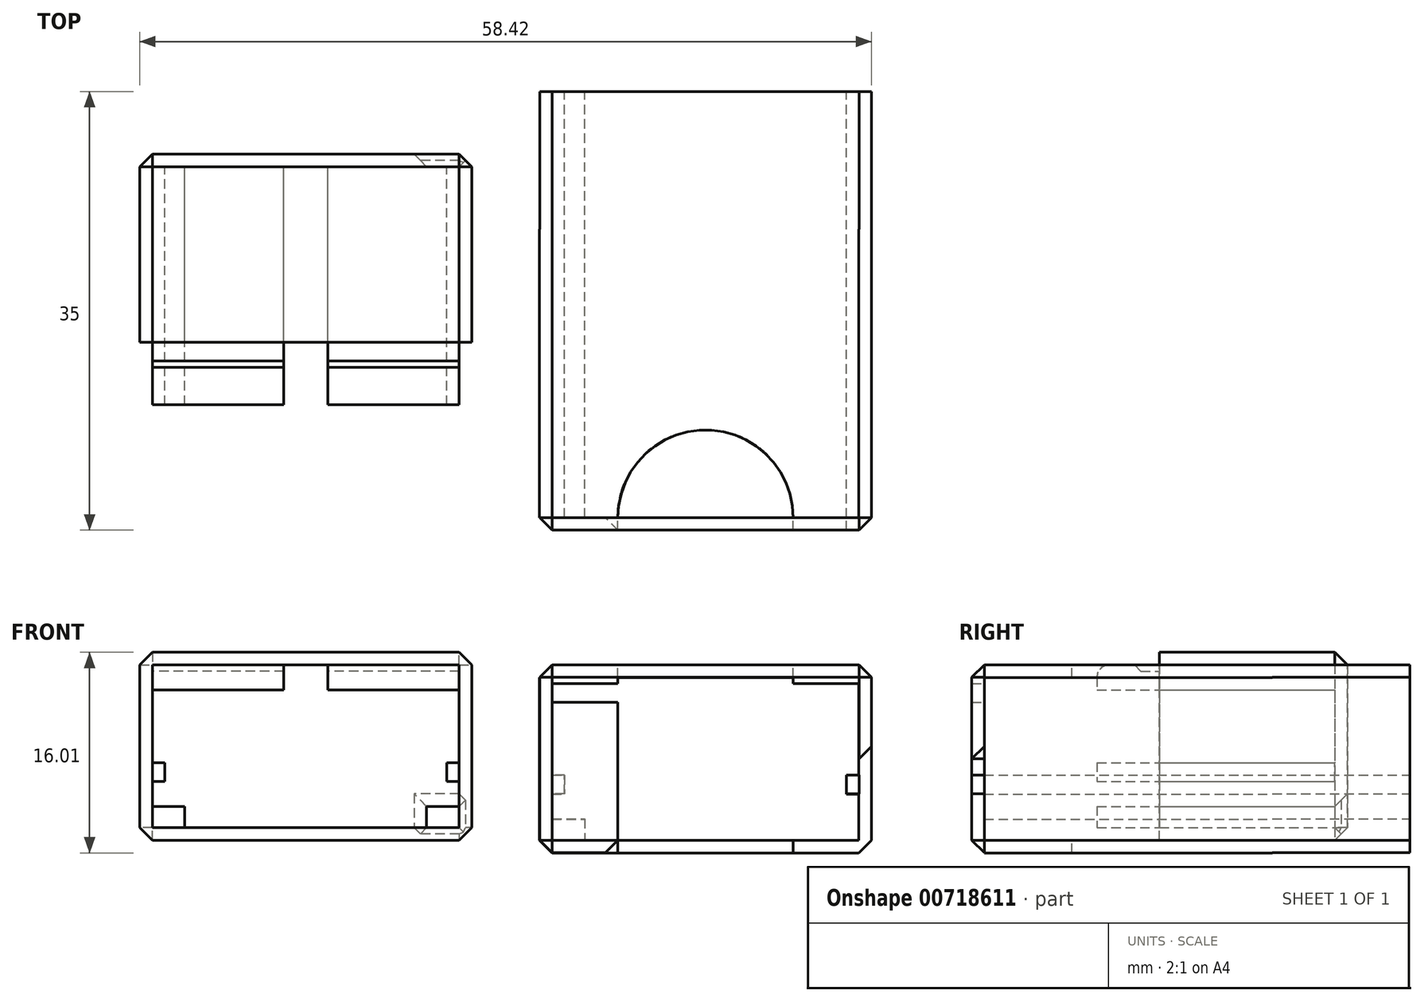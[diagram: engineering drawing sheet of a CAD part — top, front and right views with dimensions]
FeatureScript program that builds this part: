
annotation { "Feature Type Name" : "Feature", "Feature Type Description" : "" }
export const myFeature = defineFeature(function(context is Context, id is Id, definition is map)
    precondition{}
    {
        {
            var Q0;
            Q0=qCreatedBy(makeId("Front.planeOp"),FACE);
            var sketch = newSketch(context, id + "F0", { "sketchPlane" : qUnion([Q0])});
            skLineSegment(sketch, "E0.bottom", {"start": v(0, 0) * mm, "end": v(-24.5, 0) * mm});
            skLineSegment(sketch, "E0.top", {"start": v(0, -13) * mm, "end": v(-24.5, -13) * mm});
            skLineSegment(sketch, "E0.left", {"start": v(0, 0) * mm, "end": v(0, -13) * mm});
            skLineSegment(sketch, "E0.right", {"start": v(-24.5, 0) * mm, "end": v(-24.5, -13) * mm});
            skLineSegment(sketch, "E1", {"start": v(0, 0) * mm, "end": v(0, 1) * mm});
            skLineSegment(sketch, "E2", {"start": v(-25.5, 1) * mm, "end": v(-25.5, -14) * mm});
            skLineSegment(sketch, "E3", {"start": v(-25.5, -14) * mm, "end": v(1, -14) * mm});
            skLineSegment(sketch, "E4", {"start": v(1, -14) * mm, "end": v(1, 1) * mm});
            skLineSegment(sketch, "E5", {"start": v(-25.5, 1) * mm, "end": v(1, 1) * mm});
            skLineSegment(sketch, "E6", {"start": v(0, -13) * mm, "end": v(0, -9.3) * mm});
            skLineSegment(sketch, "E7", {"start": v(-24.5, -9.3) * mm, "end": v(-23.5, -9.3) * mm});
            skLineSegment(sketch, "E8", {"start": v(-23.5, -11.3) * mm, "end": v(-24.5, -11.3) * mm});
            skLineSegment(sketch, "E9", {"start": v(0, -9.3) * mm, "end": v(0, -11.3) * mm});
            skLineSegment(sketch, "E10", {"start": v(0, -11.3) * mm, "end": v(-1, -11.3) * mm});
            skLineSegment(sketch, "E11", {"start": v(-1, -9.3) * mm, "end": v(0, -9.3) * mm});
            skLineSegment(sketch, "E12", {"start": v(-23.5, -9.3) * mm, "end": v(-23.5, -7.8) * mm});
            skLineSegment(sketch, "E13", {"start": v(-23.5, -7.8) * mm, "end": v(-24.5, -7.8) * mm});
            skLineSegment(sketch, "E14", {"start": v(-24.5, -11.3) * mm, "end": v(-24.5, -9.3) * mm});
            skLineSegment(sketch, "E15", {"start": v(-1, -9.3) * mm, "end": v(-1, -7.8) * mm});
            skLineSegment(sketch, "E16", {"start": v(-1, -7.8) * mm, "end": v(0, -7.8) * mm});
            skLineSegment(sketch, "E17", {"start": v(-24.5, 0) * mm, "end": v(-24.5, -2) * mm});
            skLineSegment(sketch, "E18", {"start": v(-12.25, 0) * mm, "end": v(-10.5, 0) * mm});
            skLineSegment(sketch, "E19", {"start": v(-10.5, 0) * mm, "end": v(-14, 0) * mm});
            skLineSegment(sketch, "E20", {"start": v(-14, 0) * mm, "end": v(-14, -2) * mm});
            skLineSegment(sketch, "E21", {"start": v(-14, -2) * mm, "end": v(-24.5, -2) * mm});
            skLineSegment(sketch, "E22", {"start": v(-10.5, 0) * mm, "end": v(-10.5, -2) * mm});
            skLineSegment(sketch, "E23", {"start": v(-10.5, -2) * mm, "end": v(0, -2) * mm});
            skLineSegment(sketch, "E24", {"start": v(-24.5, -11.3) * mm, "end": v(-21.9, -11.3) * mm});
            skLineSegment(sketch, "E25", {"start": v(-21.9, -11.3) * mm, "end": v(-21.9, -13) * mm});
            skLineSegment(sketch, "E26", {"start": v(0, -11.3) * mm, "end": v(-2.6, -11.3) * mm});
            skLineSegment(sketch, "E27", {"start": v(-2.6, -11.3) * mm, "end": v(-2.6, -13) * mm});
            skLineSegment(sketch, "E28", {"start": v(0, -2) * mm, "end": v(0, -0.5) * mm});
            skLineSegment(sketch, "E29", {"start": v(0, -0.5) * mm, "end": v(-10.5, -0.5) * mm});
            skLineSegment(sketch, "E30", {"start": v(-14, -2) * mm, "end": v(-14, -0.5) * mm});
            skLineSegment(sketch, "E31", {"start": v(-14, -0.5) * mm, "end": v(-24.5, -0.5) * mm});
            skSolve(sketch);
        }
        {
            var Q0;
            Q0 = qSketchRegion(id + "F0", true);
            var Q1;
            {var subQ3=sQuery(id+"F0.wireOp",EDGE,"E20");Q1=makeQuery(id+"F0.imprint","IMPRINT",FACE,{"disambiguationData":[TD([[makeQuery(id+"F0.imprint","IMPRINT",EDGE,{"derivedFrom":subQ3}),-1.0]])]});}
            var Q2;
            {var subQ5=sQuery(id+"F0.wireOp",EDGE,"E29");Q2=makeQuery(id+"F0.imprint","IMPRINT",FACE,{"disambiguationData":[TD([[makeQuery(id+"F0.imprint","IMPRINT",EDGE,{"derivedFrom":subQ5}),-1.0]])]});}
            extrude(context, id + "F1", {"entities" : qUnion([Q0, Q1, Q2]), "depth" : 15 * mm, "offsetDistance" : 25 * mm});
        }
        {
            var Q0;
            {var subQ0=sQuery(id+"F0.wireOp",EDGE,"E21");Q0=makeQuery(id+"F0.imprint","IMPRINT",FACE,{"disambiguationData":[TD([[makeQuery(id+"F0.imprint","IMPRINT",EDGE,{"derivedFrom":subQ0}),-1.0]])]});}
            var Q1;
            {var subQ0=sQuery(id+"F0.wireOp",EDGE,"E23");Q1=makeQuery(id+"F0.imprint","IMPRINT",FACE,{"disambiguationData":[TD([[makeQuery(id+"F0.imprint","IMPRINT",EDGE,{"derivedFrom":subQ0}),1.0]])]});}
            var Q2;
            {var subQ0=sQuery(id+"F0.wireOp",EDGE,"E11");Q2=makeQuery(id+"F0.imprint","IMPRINT",FACE,{"disambiguationData":[TD([[makeQuery(id+"F0.imprint","IMPRINT",EDGE,{"derivedFrom":subQ0}),1.0]])]});}
            var Q3;
            {var subQ3=sQuery(id+"F0.wireOp",EDGE,"E6");Q3=makeQuery(id+"F0.imprint","IMPRINT",FACE,{"disambiguationData":[TD([[makeQuery(id+"F0.imprint","IMPRINT",EDGE,{"derivedFrom":subQ3}),1.0]])]});}
            var Q4;
            {var subQ0=sQuery(id+"F0.wireOp",EDGE,"E7");Q4=makeQuery(id+"F0.imprint","IMPRINT",FACE,{"disambiguationData":[TD([[makeQuery(id+"F0.imprint","IMPRINT",EDGE,{"derivedFrom":subQ0}),1.0]])]});}
            var Q5;
            {var subQ0=sQuery(id+"F0.wireOp",EDGE,"E25");Q5=makeQuery(id+"F0.imprint","IMPRINT",FACE,{"disambiguationData":[TD([[makeQuery(id+"F0.imprint","IMPRINT",EDGE,{"derivedFrom":subQ0}),-1.0]])]});}
            extrude(context, id + "F2", {"entities" : qUnion([Q0, Q1, Q2, Q3, Q4, Q5]), "operationType" : NewBodyOperationType.ADD, "depth" : 20 * mm, "offsetDistance" : 25 * mm});
        }
        {
            var Q0;
            {var subQ19=sQuery(id+"F0.wireOp",EDGE,"E2");Q0=makeQuery(id+"F0.imprint","IMPRINT",FACE,{"disambiguationData":[TD([[makeQuery(id+"F0.imprint","IMPRINT",EDGE,{"derivedFrom":subQ19}),1.0]])]});}
            var Q1;
            {var subQ3=sQuery(id+"F0.wireOp",EDGE,"E22");Q1=makeQuery(id+"F0.imprint","IMPRINT",FACE,{"disambiguationData":[TD([[makeQuery(id+"F0.imprint","IMPRINT",EDGE,{"derivedFrom":subQ3}),1.0]])]});}
            var Q2;
            {var subQ0=sQuery(id+"F0.wireOp",EDGE,"E17");Q2=makeQuery(id+"F0.imprint","IMPRINT",FACE,{"disambiguationData":[TD([[makeQuery(id+"F0.imprint","IMPRINT",EDGE,{"derivedFrom":subQ0}),1.0]])]});}
            var Q3;
            {var subQ0=sQuery(id+"F0.wireOp",EDGE,"E7");Q3=makeQuery(id+"F0.imprint","IMPRINT",FACE,{"disambiguationData":[TD([[makeQuery(id+"F0.imprint","IMPRINT",EDGE,{"derivedFrom":subQ0}),1.0]])]});}
            var Q4;
            {var subQ0=sQuery(id+"F0.wireOp",EDGE,"E25");Q4=makeQuery(id+"F0.imprint","IMPRINT",FACE,{"disambiguationData":[TD([[makeQuery(id+"F0.imprint","IMPRINT",EDGE,{"derivedFrom":subQ0}),-1.0]])]});}
            var Q5;
            {var subQ0=sQuery(id+"F0.wireOp",EDGE,"E11");Q5=makeQuery(id+"F0.imprint","IMPRINT",FACE,{"disambiguationData":[TD([[makeQuery(id+"F0.imprint","IMPRINT",EDGE,{"derivedFrom":subQ0}),1.0]])]});}
            var Q6;
            {var subQ1=sQuery(id+"F0.wireOp",EDGE,"E6");Q6=makeQuery(id+"F0.imprint","IMPRINT",FACE,{"disambiguationData":[TD([[makeQuery(id+"F0.imprint","IMPRINT",EDGE,{"derivedFrom":subQ1}),1.0]])]});}
            var Q7;
            Q7=makeQuery(id+"F0.imprint","IMPRINT",FACE,{"disambiguationData":[TD([[makeQuery(id+"F0.imprint","IMPRINT",EDGE,{"derivedFrom":sQuery(id+"F0.wireOp",EDGE,"E7")}),-1.0]])]});
            extrude(context, id + "F3", {"entities" : qUnion([Q0, Q1, Q2, Q3, Q4, Q5, Q6, Q7]), "operationType" : NewBodyOperationType.ADD, "depth" : 1 * mm, "offsetDistance" : 25 * mm});
        }
        {
            var Q0;
            {var subQ0=sQuery(id+"F0.wireOp",EDGE,"E5");var subQ1=sQuery(id+"F0.wireOp",EDGE,"E4");var subQ2=sQuery(id+"F0.wireOp",EDGE,"E3");var subQ3=sQuery(id+"F0.wireOp",EDGE,"E2");var subQ4=sQuery(id+"F0.wireOp",EDGE,"E0.right");var subQ5=sQuery(id+"F0.wireOp",EDGE,"E0.left");var subQ6=sQuery(id+"F0.wireOp",EDGE,"E0.top");var subQ7=sQuery(id+"F0.wireOp",EDGE,"E6");var subQ8=sQuery(id+"F0.wireOp",EDGE,"E17");var subQ9=sQuery(id+"F0.wireOp",EDGE,"E0.bottom");Q0=makeQuery(id+"F3.boolean.opBoolean","MERGE",FACE,{"derivedFrom":[makeQuery(id+"F2.boolean.opBoolean","MERGE",FACE,{"derivedFrom":[makeQuery(id+"F1.opExtrude","CAP_FACE",FACE,{"disambiguationData":[OSD([subQ9,subQ6,subQ5,subQ4,subQ3,subQ2,subQ1,subQ0,subQ7,sQuery(id+"F0.wireOp",EDGE,"E9"),sQuery(id+"F0.wireOp",EDGE,"E14"),subQ8,sQuery(id+"F0.wireOp",EDGE,"E19")])],"isStart":true}),makeQuery(id+"F2.opExtrude","CAP_FACE",FACE,{"disambiguationData":[OSD([subQ9,subQ5,sQuery(id+"F0.wireOp",EDGE,"E22"),sQuery(id+"F0.wireOp",EDGE,"E23")])],"isStart":true}),makeQuery(id+"F2.opExtrude","CAP_FACE",FACE,{"disambiguationData":[OSD([subQ9,subQ8,sQuery(id+"F0.wireOp",EDGE,"E20"),sQuery(id+"F0.wireOp",EDGE,"E21")])],"isStart":true}),makeQuery(id+"F2.opExtrude","CAP_FACE",FACE,{"disambiguationData":[OSD([subQ6,subQ7,sQuery(id+"F0.wireOp",EDGE,"E26"),sQuery(id+"F0.wireOp",EDGE,"E27")])],"isStart":true}),makeQuery(id+"F2.opExtrude","CAP_FACE",FACE,{"disambiguationData":[OSD([subQ6,subQ4,sQuery(id+"F0.wireOp",EDGE,"E24"),sQuery(id+"F0.wireOp",EDGE,"E25")])],"isStart":true}),makeQuery(id+"F2.opExtrude","CAP_FACE",FACE,{"disambiguationData":[OSD([subQ5,sQuery(id+"F0.wireOp",EDGE,"E11"),sQuery(id+"F0.wireOp",EDGE,"E15"),sQuery(id+"F0.wireOp",EDGE,"E16")])],"isStart":true}),makeQuery(id+"F2.opExtrude","CAP_FACE",FACE,{"disambiguationData":[OSD([subQ4,sQuery(id+"F0.wireOp",EDGE,"E7"),sQuery(id+"F0.wireOp",EDGE,"E12"),sQuery(id+"F0.wireOp",EDGE,"E13")])],"isStart":true})]}),makeQuery(id+"F3.opExtrude","CAP_FACE",FACE,{"disambiguationData":[OSD([subQ3,subQ2,subQ1,subQ0])],"isStart":true})]});}
            var Q1;
            Q1=makeQuery(id+"F1.opExtrude","SWEPT_EDGE",EDGE,{"disambiguationData":[OSD([sQuery(id+"F0.wireOp",EDGE,"E2"),sQuery(id+"F0.wireOp",EDGE,"E3")])]});
            var Q2;
            Q2=makeQuery(id+"F1.opExtrude","SWEPT_EDGE",EDGE,{"disambiguationData":[OSD([sQuery(id+"F0.wireOp",EDGE,"E3"),sQuery(id+"F0.wireOp",EDGE,"E4")])]});
            var Q3;
            Q3=makeQuery(id+"F1.opExtrude","SWEPT_EDGE",EDGE,{"disambiguationData":[OSD([sQuery(id+"F0.wireOp",EDGE,"E2"),sQuery(id+"F0.wireOp",EDGE,"E5")])]});
            var Q4;
            Q4=makeQuery(id+"F1.opExtrude","SWEPT_EDGE",EDGE,{"disambiguationData":[OSD([sQuery(id+"F0.wireOp",EDGE,"E4"),sQuery(id+"F0.wireOp",EDGE,"E5")])]});
            chamfer(context, id + "F4", {"entities" : qUnion([Q0, Q1, Q2, Q3, Q4]), "width" : 1 * mm, "tangentPropagation" : true});
        }
        {
            var Q0;
            Q0=qCreatedBy(makeId("Front.planeOp"),FACE);
            cPlane(context, id + "F5", {"entities" : qUnion([Q0]), "cplaneType" : CPlaneType.OFFSET, "offset" : 16 * mm, "width" : 150 * mm, "height" : 150 * mm});
        }
        {
            var Q0;
            Q0=qCreatedBy(id+"F5.planeOp",FACE);
            var sketch = newSketch(context, id + "F6", { "sketchPlane" : qUnion([Q0])});
            skLineSegment(sketch, "E32.bottom", {"start": v(0, 0) * mm, "end": v(-10.5, 0) * mm});
            skLineSegment(sketch, "E32.top", {"start": v(0, -2) * mm, "end": v(-10.5, -2) * mm});
            skLineSegment(sketch, "E32.left", {"start": v(0, 0) * mm, "end": v(0, -2) * mm});
            skLineSegment(sketch, "E32.right", {"start": v(-10.5, 0) * mm, "end": v(-10.5, -2) * mm});
            skLineSegment(sketch, "E33", {"start": v(-10.5, 0) * mm, "end": v(-14, 0) * mm});
            skLineSegment(sketch, "E34.bottom", {"start": v(-14, 0) * mm, "end": v(-24.5, 0) * mm});
            skLineSegment(sketch, "E34.top", {"start": v(-14, -2) * mm, "end": v(-24.5, -2) * mm});
            skLineSegment(sketch, "E34.left", {"start": v(-14, 0) * mm, "end": v(-14, -2) * mm});
            skLineSegment(sketch, "E34.right", {"start": v(-24.5, 0) * mm, "end": v(-24.5, -2) * mm});
            skSolve(sketch);
        }
        {
            var Q0;
            Q0 = qSketchRegion(id + "F6", true);
            extrude(context, id + "F7", {"entities" : qUnion([Q0]), "operationType" : NewBodyOperationType.ADD, "depth" : 4 * mm, "offsetDistance" : 25 * mm});
        }
        {
            var Q0;
            Q0=makeQuery(id+"F7.opExtrude","CAP_EDGE",EDGE,{"disambiguationData":[OSD([sQuery(id+"F6.wireOp",EDGE,"E32.bottom")])],"isStart":false});
            var Q1;
            Q1=makeQuery(id+"F7.opExtrude","CAP_EDGE",EDGE,{"disambiguationData":[OSD([sQuery(id+"F6.wireOp",EDGE,"E34.bottom")])],"isStart":false});
            fillet(context, id + "F8", {"entities" : qUnion([Q0, Q1]), "radius" : 1 * mm, "tangentPropagation" : true, "allowEdgeOverflow" : false});
        }
        {
            var Q0;
            Q0=makeQuery(id+"F7.opExtrude","CAP_EDGE",EDGE,{"disambiguationData":[OSD([sQuery(id+"F6.wireOp",EDGE,"E32.bottom")])],"isStart":true});
            var Q1;
            Q1=makeQuery(id+"F7.opExtrude","CAP_EDGE",EDGE,{"disambiguationData":[OSD([sQuery(id+"F6.wireOp",EDGE,"E34.bottom")])],"isStart":true});
            chamfer(context, id + "F9", {"entities" : qUnion([Q0, Q1]), "width" : 1 * mm, "tangentPropagation" : true});
        }
        {
            var Q0;
            Q0=qCreatedBy(makeId("Front.planeOp"),FACE);
            var sketch = newSketch(context, id + "F10", { "sketchPlane" : qUnion([Q0])});
            skLineSegment(sketch, "E35.bottom", {"start": v(6.42, 0) * mm, "end": v(32.92, 0) * mm});
            skLineSegment(sketch, "E35.top", {"start": v(6.42, -15) * mm, "end": v(32.92, -15) * mm});
            skLineSegment(sketch, "E35.left", {"start": v(6.42, 0) * mm, "end": v(6.42, -15) * mm});
            skLineSegment(sketch, "E35.right", {"start": v(32.92, 0) * mm, "end": v(32.92, -15) * mm});
            skLineSegment(sketch, "E36", {"start": v(7.42, 0) * mm, "end": v(7.42, -1) * mm});
            skLineSegment(sketch, "E37", {"start": v(7.42, -14) * mm, "end": v(6.42, -14) * mm});
            skLineSegment(sketch, "E38", {"start": v(7.42, -1) * mm, "end": v(7.42, -14) * mm});
            skLineSegment(sketch, "E39.bottom", {"start": v(31.92, -1) * mm, "end": v(7.42, -1) * mm});
            skLineSegment(sketch, "E39.top", {"start": v(31.92, -14) * mm, "end": v(7.42, -14) * mm});
            skLineSegment(sketch, "E39.left", {"start": v(31.92, -1) * mm, "end": v(31.92, -14) * mm});
            skLineSegment(sketch, "E40", {"start": v(31.92, -14) * mm, "end": v(31.92, -10.3) * mm});
            skLineSegment(sketch, "E41", {"start": v(31.92, -10.3) * mm, "end": v(31.92, -12.3) * mm});
            skLineSegment(sketch, "E42", {"start": v(31.92, -10.3) * mm, "end": v(30.92, -10.3) * mm});
            skLineSegment(sketch, "E43", {"start": v(32.92, -7.5) * mm, "end": v(31.92, -7.5) * mm});
            skLineSegment(sketch, "E44", {"start": v(30.92, -10.3) * mm, "end": v(30.92, -8.8) * mm});
            skLineSegment(sketch, "E45", {"start": v(30.92, -8.8) * mm, "end": v(31.92, -8.8) * mm});
            skLineSegment(sketch, "E46", {"start": v(31.92, -14) * mm, "end": v(29.32, -14) * mm});
            skLineSegment(sketch, "E47", {"start": v(31.92, -12.3) * mm, "end": v(29.32, -12.3) * mm});
            skLineSegment(sketch, "E48", {"start": v(29.32, -12.3) * mm, "end": v(29.32, -14) * mm});
            skLineSegment(sketch, "E49", {"start": v(19.67, -1) * mm, "end": v(19.67, -14) * mm});
            skLineSegment(sketch, "E50.MirrorCS", {"start": v(8.42, -8.8) * mm, "end": v(7.42, -8.8) * mm});
            skLineSegment(sketch, "E51.MirrorCS", {"start": v(8.42, -10.3) * mm, "end": v(8.42, -8.8) * mm});
            skLineSegment(sketch, "E52.MirrorCS", {"start": v(7.42, -10.3) * mm, "end": v(8.42, -10.3) * mm});
            skLineSegment(sketch, "E53.MirrorCS", {"start": v(7.42, -12.3) * mm, "end": v(10.02, -12.3) * mm});
            skLineSegment(sketch, "E54.MirrorCS", {"start": v(10.02, -12.3) * mm, "end": v(10.02, -14) * mm});
            skLineSegment(sketch, "E55", {"start": v(19.67, -1) * mm, "end": v(19.67, -3) * mm});
            skLineSegment(sketch, "E56", {"start": v(17.92, -3) * mm, "end": v(17.92, -1) * mm});
            skLineSegment(sketch, "E57", {"start": v(17.92, -1) * mm, "end": v(17.92, -1.5) * mm});
            skLineSegment(sketch, "E58", {"start": v(17.92, -1.5) * mm, "end": v(7.42, -1.5) * mm});
            skLineSegment(sketch, "E59", {"start": v(7.42, -1.5) * mm, "end": v(7.42, -3) * mm});
            skLineSegment(sketch, "E60", {"start": v(31.92, -3) * mm, "end": v(31.92, -1.5) * mm});
            skLineSegment(sketch, "E61", {"start": v(31.92, -1.5) * mm, "end": v(21.42, -1.5) * mm});
            skLineSegment(sketch, "E62", {"start": v(21.42, -1.5) * mm, "end": v(21.42, -3) * mm});
            skLineSegment(sketch, "E63", {"start": v(21.42, -1.5) * mm, "end": v(21.42, -1) * mm});
            skLineSegment(sketch, "E64", {"start": v(21.42, -1) * mm, "end": v(21.42, -3) * mm});
            skLineSegment(sketch, "E65", {"start": v(7.42, -3) * mm, "end": v(17.92, -3) * mm});
            skLineSegment(sketch, "E66", {"start": v(21.42, -3) * mm, "end": v(31.92, -3) * mm});
            skSolve(sketch);
        }
        {
            var Q0;
            {var subQ10=sQuery(id+"F10.wireOp",EDGE,"E36");Q0=makeQuery(id+"F10.imprint","IMPRINT",FACE,{"disambiguationData":[TD([[makeQuery(id+"F10.imprint","IMPRINT",EDGE,{"derivedFrom":subQ10}),1.0]])]});}
            var Q1;
            {var subQ3=sQuery(id+"F10.wireOp",EDGE,"E35.top");Q1=makeQuery(id+"F10.imprint","IMPRINT",FACE,{"disambiguationData":[TD([[makeQuery(id+"F10.imprint","IMPRINT",EDGE,{"derivedFrom":subQ3}),1.0]])]});}
            var Q2;
            {var subQ0=sQuery(id+"F10.wireOp",EDGE,"E36");Q2=makeQuery(id+"F10.imprint","IMPRINT",FACE,{"disambiguationData":[TD([[makeQuery(id+"F10.imprint","IMPRINT",EDGE,{"derivedFrom":subQ0}),-1.0]])]});}
            var Q3;
            {var subQ0=sQuery(id+"F10.wireOp",EDGE,"E42");Q3=makeQuery(id+"F10.imprint","IMPRINT",FACE,{"disambiguationData":[TD([[makeQuery(id+"F10.imprint","IMPRINT",EDGE,{"derivedFrom":subQ0}),-1.0]])]});}
            var Q4;
            Q4=makeQuery(id+"F10.imprint","IMPRINT",FACE,{"disambiguationData":[TD([[makeQuery(id+"F10.imprint","IMPRINT",EDGE,{"derivedFrom":sQuery(id+"F10.wireOp",EDGE,"E40")}),1.0]])]});
            var Q5;
            {var subQ0=sQuery(id+"F10.wireOp",EDGE,"E50.MirrorCS");Q5=makeQuery(id+"F10.imprint","IMPRINT",FACE,{"disambiguationData":[TD([[makeQuery(id+"F10.imprint","IMPRINT",EDGE,{"derivedFrom":subQ0}),1.0]])]});}
            var Q6;
            {var subQ4=sQuery(id+"F10.wireOp",EDGE,"E53.MirrorCS");Q6=makeQuery(id+"F10.imprint","IMPRINT",FACE,{"disambiguationData":[TD([[makeQuery(id+"F10.imprint","IMPRINT",EDGE,{"derivedFrom":subQ4}),-1.0]])]});}
            var Q7;
            Q7=sQuery(id+"F10.wireOp",EDGE,"E35.bottom");
            var Q8;
            Q8=sQuery(id+"F10.wireOp",EDGE,"E35.right");
            var Q9;
            Q9=sQuery(id+"F10.wireOp",EDGE,"E39.left");
            extrude(context, id + "F11", {"entities" : qUnion([Q0, Q1, Q2, Q3, Q4, Q5, Q6]), "surfaceEntities" : qUnion([Q7, Q8, Q9]), "depth" : 6 * mm, "offsetDistance" : 25 * mm});
        }
        {
            var Q0;
            Q0=qCreatedBy(makeId("Front.planeOp"),FACE);
            cPlane(context, id + "F12", {"entities" : qUnion([Q0]), "cplaneType" : CPlaneType.OFFSET, "offset" : 6 * mm, "width" : 150 * mm, "height" : 150 * mm});
        }
        {
            var Q0;
            Q0=qCreatedBy(id+"F12.planeOp",FACE);
            var sketch = newSketch(context, id + "F13", { "sketchPlane" : qUnion([Q0])});
            skLineSegment(sketch, "E67.bottom", {"start": v(6.42, 0) * mm, "end": v(32.92, 0) * mm});
            skLineSegment(sketch, "E67.top", {"start": v(6.42, -15) * mm, "end": v(32.92, -15) * mm});
            skLineSegment(sketch, "E67.left", {"start": v(6.42, 0) * mm, "end": v(6.42, -15) * mm});
            skLineSegment(sketch, "E67.right", {"start": v(32.92, 0) * mm, "end": v(32.92, -15) * mm});
            skLineSegment(sketch, "E68", {"start": v(7.42, 0) * mm, "end": v(7.42, -1) * mm});
            skLineSegment(sketch, "E69", {"start": v(7.42, -14) * mm, "end": v(6.42, -14) * mm});
            skLineSegment(sketch, "E70", {"start": v(7.42, -1) * mm, "end": v(7.42, -14) * mm});
            skLineSegment(sketch, "E71.bottom", {"start": v(31.92, -1) * mm, "end": v(7.42, -1) * mm});
            skLineSegment(sketch, "E71.top", {"start": v(31.92, -14) * mm, "end": v(7.42, -14) * mm});
            skLineSegment(sketch, "E71.left", {"start": v(31.92, -1) * mm, "end": v(31.92, -14) * mm});
            skLineSegment(sketch, "E72", {"start": v(31.92, -14) * mm, "end": v(31.92, -10.3) * mm});
            skLineSegment(sketch, "E73", {"start": v(31.92, -10.3) * mm, "end": v(31.92, -12.3) * mm});
            skLineSegment(sketch, "E74", {"start": v(31.92, -10.3) * mm, "end": v(30.92, -10.3) * mm});
            skLineSegment(sketch, "E75", {"start": v(32.92, -7.5) * mm, "end": v(31.92, -7.5) * mm});
            skLineSegment(sketch, "E76", {"start": v(30.92, -10.3) * mm, "end": v(30.92, -8.8) * mm});
            skLineSegment(sketch, "E77", {"start": v(30.92, -8.8) * mm, "end": v(31.92, -8.8) * mm});
            skLineSegment(sketch, "E78", {"start": v(31.92, -14) * mm, "end": v(29.32, -14) * mm});
            skLineSegment(sketch, "E79", {"start": v(31.92, -12.3) * mm, "end": v(29.32, -12.3) * mm});
            skLineSegment(sketch, "E80", {"start": v(29.32, -12.3) * mm, "end": v(29.32, -14) * mm});
            skLineSegment(sketch, "E81", {"start": v(19.67, -1) * mm, "end": v(19.67, -14) * mm});
            skLineSegment(sketch, "E82.MirrorCS", {"start": v(8.42, -8.8) * mm, "end": v(7.42, -8.8) * mm});
            skLineSegment(sketch, "E83.MirrorCS", {"start": v(8.42, -10.3) * mm, "end": v(8.42, -8.8) * mm});
            skLineSegment(sketch, "E84.MirrorCS", {"start": v(7.42, -10.3) * mm, "end": v(8.42, -10.3) * mm});
            skLineSegment(sketch, "E85.MirrorCS", {"start": v(7.42, -12.3) * mm, "end": v(10.02, -12.3) * mm});
            skLineSegment(sketch, "E86.MirrorCS", {"start": v(10.02, -12.3) * mm, "end": v(10.02, -14) * mm});
            skLineSegment(sketch, "E87", {"start": v(19.67, -1) * mm, "end": v(19.67, -3) * mm});
            skLineSegment(sketch, "E88", {"start": v(17.92, -3) * mm, "end": v(17.92, -1) * mm});
            skLineSegment(sketch, "E89", {"start": v(17.92, -1) * mm, "end": v(17.92, -1.5) * mm});
            skLineSegment(sketch, "E90", {"start": v(17.92, -1.5) * mm, "end": v(7.42, -1.5) * mm});
            skLineSegment(sketch, "E91", {"start": v(7.42, -1.5) * mm, "end": v(7.42, -3) * mm});
            skLineSegment(sketch, "E92", {"start": v(31.92, -3) * mm, "end": v(31.92, -1.5) * mm});
            skLineSegment(sketch, "E93", {"start": v(31.92, -1.5) * mm, "end": v(21.42, -1.5) * mm});
            skLineSegment(sketch, "E94", {"start": v(21.42, -1.5) * mm, "end": v(21.42, -3) * mm});
            skLineSegment(sketch, "E95", {"start": v(21.42, -1.5) * mm, "end": v(21.42, -1) * mm});
            skLineSegment(sketch, "E96", {"start": v(21.42, -1) * mm, "end": v(21.42, -3) * mm});
            skLineSegment(sketch, "E97", {"start": v(7.42, -3) * mm, "end": v(17.92, -3) * mm});
            skLineSegment(sketch, "E98", {"start": v(21.42, -3) * mm, "end": v(31.92, -3) * mm});
            skSolve(sketch);
        }
        {
            var Q0;
            Q0 = qSketchRegion(id + "F13", true);
            var Q1;
            {var subQ0=sQuery(id+"F13.wireOp",EDGE,"E74");Q1=makeQuery(id+"F13.imprint","IMPRINT",FACE,{"disambiguationData":[TD([[makeQuery(id+"F13.imprint","IMPRINT",EDGE,{"derivedFrom":subQ0}),-1.0]])]});}
            var Q2;
            Q2=makeQuery(id+"F13.imprint","IMPRINT",FACE,{"disambiguationData":[TD([[makeQuery(id+"F13.imprint","IMPRINT",EDGE,{"derivedFrom":sQuery(id+"F13.wireOp",EDGE,"E72")}),1.0]])]});
            var Q3;
            {var subQ0=sQuery(id+"F13.wireOp",EDGE,"E82.MirrorCS");Q3=makeQuery(id+"F13.imprint","IMPRINT",FACE,{"disambiguationData":[TD([[makeQuery(id+"F13.imprint","IMPRINT",EDGE,{"derivedFrom":subQ0}),1.0]])]});}
            var Q4;
            {var subQ4=sQuery(id+"F13.wireOp",EDGE,"E85.MirrorCS");Q4=makeQuery(id+"F13.imprint","IMPRINT",FACE,{"disambiguationData":[TD([[makeQuery(id+"F13.imprint","IMPRINT",EDGE,{"derivedFrom":subQ4}),-1.0]])]});}
            extrude(context, id + "F14", {"entities" : qUnion([Q0, Q1, Q2, Q3, Q4]), "operationType" : NewBodyOperationType.ADD, "depth" : 23 * mm, "offsetDistance" : 25 * mm});
        }
        {
            var Q0;
            Q0=qCreatedBy(makeId("Front.planeOp"),FACE);
            cPlane(context, id + "F15", {"entities" : qUnion([Q0]), "cplaneType" : CPlaneType.OFFSET, "offset" : 29 * mm, "width" : 150 * mm, "height" : 150 * mm});
        }
        {
            var Q0;
            Q0=qCreatedBy(id+"F15.planeOp",FACE);
            var sketch = newSketch(context, id + "F16", { "sketchPlane" : qUnion([Q0])});
            skLineSegment(sketch, "E99.bottom", {"start": v(6.42, 0) * mm, "end": v(32.92, 0) * mm});
            skLineSegment(sketch, "E99.top", {"start": v(6.42, -15) * mm, "end": v(32.92, -15) * mm});
            skLineSegment(sketch, "E99.left", {"start": v(6.42, 0) * mm, "end": v(6.42, -15) * mm});
            skLineSegment(sketch, "E99.right", {"start": v(32.92, 0) * mm, "end": v(32.92, -15) * mm});
            skLineSegment(sketch, "E100", {"start": v(7.42, 0) * mm, "end": v(7.42, -1) * mm});
            skLineSegment(sketch, "E101", {"start": v(7.42, -14) * mm, "end": v(6.42, -14) * mm});
            skLineSegment(sketch, "E102", {"start": v(7.42, -1) * mm, "end": v(7.42, -14) * mm});
            skLineSegment(sketch, "E103.bottom", {"start": v(31.92, -1) * mm, "end": v(7.42, -1) * mm});
            skLineSegment(sketch, "E103.top", {"start": v(31.92, -14) * mm, "end": v(7.42, -14) * mm});
            skLineSegment(sketch, "E103.left", {"start": v(31.92, -1) * mm, "end": v(31.92, -14) * mm});
            skLineSegment(sketch, "E104", {"start": v(31.92, -14) * mm, "end": v(31.92, -10.3) * mm});
            skLineSegment(sketch, "E105", {"start": v(31.92, -10.3) * mm, "end": v(31.92, -12.3) * mm});
            skLineSegment(sketch, "E106", {"start": v(31.92, -10.3) * mm, "end": v(30.92, -10.3) * mm});
            skLineSegment(sketch, "E107", {"start": v(32.92, -7.5) * mm, "end": v(31.92, -7.5) * mm});
            skLineSegment(sketch, "E108", {"start": v(30.92, -10.3) * mm, "end": v(30.92, -8.8) * mm});
            skLineSegment(sketch, "E109", {"start": v(30.92, -8.8) * mm, "end": v(31.92, -8.8) * mm});
            skLineSegment(sketch, "E110", {"start": v(31.92, -14) * mm, "end": v(29.32, -14) * mm});
            skLineSegment(sketch, "E111", {"start": v(31.92, -12.3) * mm, "end": v(29.32, -12.3) * mm});
            skLineSegment(sketch, "E112", {"start": v(29.32, -12.3) * mm, "end": v(29.32, -14) * mm});
            skLineSegment(sketch, "E113", {"start": v(19.67, -1) * mm, "end": v(19.67, -14) * mm});
            skLineSegment(sketch, "E114.MirrorCS", {"start": v(8.42, -8.8) * mm, "end": v(7.42, -8.8) * mm});
            skLineSegment(sketch, "E115.MirrorCS", {"start": v(8.42, -10.3) * mm, "end": v(8.42, -8.8) * mm});
            skLineSegment(sketch, "E116.MirrorCS", {"start": v(7.42, -10.3) * mm, "end": v(8.42, -10.3) * mm});
            skLineSegment(sketch, "E117.MirrorCS", {"start": v(7.42, -12.3) * mm, "end": v(10.02, -12.3) * mm});
            skLineSegment(sketch, "E118.MirrorCS", {"start": v(10.02, -12.3) * mm, "end": v(10.02, -14) * mm});
            skLineSegment(sketch, "E119", {"start": v(19.67, -1) * mm, "end": v(19.67, -3) * mm});
            skLineSegment(sketch, "E120", {"start": v(17.92, -3) * mm, "end": v(17.92, -1) * mm});
            skLineSegment(sketch, "E121", {"start": v(17.92, -1) * mm, "end": v(17.92, -1.5) * mm});
            skLineSegment(sketch, "E122", {"start": v(17.92, -1.5) * mm, "end": v(7.42, -1.5) * mm});
            skLineSegment(sketch, "E123", {"start": v(7.42, -1.5) * mm, "end": v(7.42, -3) * mm});
            skLineSegment(sketch, "E124", {"start": v(31.92, -3) * mm, "end": v(31.92, -1.5) * mm});
            skLineSegment(sketch, "E125", {"start": v(31.92, -1.5) * mm, "end": v(21.42, -1.5) * mm});
            skLineSegment(sketch, "E126", {"start": v(21.42, -1.5) * mm, "end": v(21.42, -3) * mm});
            skLineSegment(sketch, "E127", {"start": v(21.42, -1.5) * mm, "end": v(21.42, -1) * mm});
            skLineSegment(sketch, "E128", {"start": v(21.42, -1) * mm, "end": v(21.42, -3) * mm});
            skLineSegment(sketch, "E129", {"start": v(7.42, -3) * mm, "end": v(17.92, -3) * mm});
            skLineSegment(sketch, "E130", {"start": v(21.42, -3) * mm, "end": v(31.92, -3) * mm});
            skLineSegment(sketch, "E131", {"start": v(19.67, 0) * mm, "end": v(26.67, 0) * mm});
            skLineSegment(sketch, "E132", {"start": v(26.67, 0) * mm, "end": v(26.67, -15) * mm});
            skLineSegment(sketch, "E133", {"start": v(26.67, -15) * mm, "end": v(12.67, -15) * mm});
            skLineSegment(sketch, "E134", {"start": v(12.67, -15) * mm, "end": v(12.67, 0) * mm});
            skSolve(sketch);
        }
        {
            var Q0;
            {var subQ9=sQuery(id+"F16.wireOp",EDGE,"E107");Q0=makeQuery(id+"F16.imprint","IMPRINT",FACE,{"disambiguationData":[TD([[makeQuery(id+"F16.imprint","IMPRINT",EDGE,{"derivedFrom":subQ9}),-1.0]])]});}
            var Q1;
            {var subQ0=sQuery(id+"F16.wireOp",EDGE,"E124");Q1=makeQuery(id+"F16.imprint","IMPRINT",FACE,{"disambiguationData":[TD([[makeQuery(id+"F16.imprint","IMPRINT",EDGE,{"derivedFrom":subQ0}),1.0]])]});}
            var Q2;
            {var subQ0=sQuery(id+"F16.wireOp",EDGE,"E103.left");var subQ1=sQuery(id+"F16.wireOp",EDGE,"E103.bottom");var subQ2=makeQuery(id+"F16.imprint","INTERSECT",VERTEX,{"derivedFrom":[subQ1,subQ0]});Q2=makeQuery(id+"F16.imprint","IMPRINT",FACE,{"disambiguationData":[TD([[makeQuery(id+"F16.imprint","IMPRINT",EDGE,{"disambiguationData":[TD([[subQ2,-1.0]])],"derivedFrom":subQ1}),1.0]])]});}
            var Q3;
            Q3=makeQuery(id+"F16.imprint","IMPRINT",FACE,{"disambiguationData":[TD([[makeQuery(id+"F16.imprint","IMPRINT",EDGE,{"derivedFrom":sQuery(id+"F16.wireOp",EDGE,"E104")}),-1.0]])]});
            var Q4;
            Q4=makeQuery(id+"F16.imprint","IMPRINT",FACE,{"disambiguationData":[TD([[makeQuery(id+"F16.imprint","IMPRINT",EDGE,{"derivedFrom":sQuery(id+"F16.wireOp",EDGE,"E105")}),-1.0]])]});
            var Q5;
            {var subQ0=sQuery(id+"F16.wireOp",EDGE,"E106");Q5=makeQuery(id+"F16.imprint","IMPRINT",FACE,{"disambiguationData":[TD([[makeQuery(id+"F16.imprint","IMPRINT",EDGE,{"derivedFrom":subQ0}),-1.0]])]});}
            var Q6;
            Q6=makeQuery(id+"F16.imprint","IMPRINT",FACE,{"disambiguationData":[TD([[makeQuery(id+"F16.imprint","IMPRINT",EDGE,{"derivedFrom":sQuery(id+"F16.wireOp",EDGE,"E104")}),1.0]])]});
            var Q7;
            {var subQ0=sQuery(id+"F16.wireOp",EDGE,"E114.MirrorCS");Q7=makeQuery(id+"F16.imprint","IMPRINT",FACE,{"disambiguationData":[TD([[makeQuery(id+"F16.imprint","IMPRINT",EDGE,{"derivedFrom":subQ0}),-1.0]])]});}
            var Q8;
            {var subQ0=sQuery(id+"F16.wireOp",EDGE,"E123");Q8=makeQuery(id+"F16.imprint","IMPRINT",FACE,{"disambiguationData":[TD([[makeQuery(id+"F16.imprint","IMPRINT",EDGE,{"derivedFrom":subQ0}),1.0]])]});}
            var Q9;
            {var subQ1=sQuery(id+"F16.wireOp",EDGE,"E103.bottom");var subQ3=sQuery(id+"F16.wireOp",EDGE,"E134");var subQ4=makeQuery(id+"F16.imprint","INTERSECT",VERTEX,{"derivedFrom":[subQ1,subQ3]});Q9=makeQuery(id+"F16.imprint","IMPRINT",FACE,{"disambiguationData":[TD([[makeQuery(id+"F16.imprint","IMPRINT",EDGE,{"disambiguationData":[TD([[subQ4,1.0]])],"derivedFrom":subQ3}),1.0]])]});}
            var Q10;
            {var subQ0=sQuery(id+"F16.wireOp",EDGE,"E100");Q10=makeQuery(id+"F16.imprint","IMPRINT",FACE,{"disambiguationData":[TD([[makeQuery(id+"F16.imprint","IMPRINT",EDGE,{"derivedFrom":subQ0}),1.0]])]});}
            var Q11;
            {var subQ4=sQuery(id+"F16.wireOp",EDGE,"E100");Q11=makeQuery(id+"F16.imprint","IMPRINT",FACE,{"disambiguationData":[TD([[makeQuery(id+"F16.imprint","IMPRINT",EDGE,{"derivedFrom":subQ4}),-1.0]])]});}
            var Q12;
            {var subQ4=sQuery(id+"F16.wireOp",EDGE,"E117.MirrorCS");Q12=makeQuery(id+"F16.imprint","IMPRINT",FACE,{"disambiguationData":[TD([[makeQuery(id+"F16.imprint","IMPRINT",EDGE,{"derivedFrom":subQ4}),-1.0]])]});}
            var Q13;
            {var subQ4=sQuery(id+"F16.wireOp",EDGE,"E101");Q13=makeQuery(id+"F16.imprint","IMPRINT",FACE,{"disambiguationData":[TD([[makeQuery(id+"F16.imprint","IMPRINT",EDGE,{"derivedFrom":subQ4}),1.0]])]});}
            var Q14;
            {var subQ0=sQuery(id+"F16.wireOp",EDGE,"E114.MirrorCS");Q14=makeQuery(id+"F16.imprint","IMPRINT",FACE,{"disambiguationData":[TD([[makeQuery(id+"F16.imprint","IMPRINT",EDGE,{"derivedFrom":subQ0}),1.0]])]});}
            extrude(context, id + "F17", {"entities" : qUnion([Q0, Q1, Q2, Q3, Q4, Q5, Q6, Q7, Q8, Q9, Q10, Q11, Q12, Q13, Q14]), "depth" : 1 * mm, "offsetDistance" : 25 * mm});
        }
        {
            var Q0;
            Q0=makeQuery(id+"F17.opExtrude","CAP_EDGE",EDGE,{"disambiguationData":[OSD([sQuery(id+"F16.wireOp",EDGE,"E99.right")])],"isStart":false});
            var Q1;
            {var subQ0=sQuery(id+"F16.wireOp",EDGE,"E99.bottom");Q1=makeQuery(id+"F17.opExtrude","CAP_EDGE",EDGE,{"disambiguationData":[OSD([subQ0]),TDD([makeQuery(id+"F16.imprint","IMPRINT",EDGE,{"disambiguationData":[TD([[makeQuery(id+"F16.imprint","INTERSECT",VERTEX,{"derivedFrom":[subQ0,sQuery(id+"F16.wireOp",EDGE,"E99.right")]}),1.0]])],"derivedFrom":subQ0})])],"isStart":false});}
            var Q2;
            {var subQ0=sQuery(id+"F16.wireOp",EDGE,"E99.top");Q2=makeQuery(id+"F17.opExtrude","CAP_EDGE",EDGE,{"disambiguationData":[OSD([subQ0]),TDD([makeQuery(id+"F16.imprint","IMPRINT",EDGE,{"disambiguationData":[TD([[makeQuery(id+"F16.imprint","INTERSECT",VERTEX,{"derivedFrom":[subQ0,sQuery(id+"F16.wireOp",EDGE,"E99.right")]}),1.0]])],"derivedFrom":subQ0})])],"isStart":false});}
            var Q3;
            {var subQ0=sQuery(id+"F16.wireOp",EDGE,"E99.top");Q3=makeQuery(id+"F17.opExtrude","CAP_EDGE",EDGE,{"disambiguationData":[OSD([subQ0]),TDD([makeQuery(id+"F16.imprint","IMPRINT",EDGE,{"disambiguationData":[TD([[makeQuery(id+"F16.imprint","INTERSECT",VERTEX,{"derivedFrom":[subQ0,sQuery(id+"F16.wireOp",EDGE,"E99.left")]}),-1.0]])],"derivedFrom":subQ0})])],"isStart":false});}
            var Q4;
            Q4=makeQuery(id+"F17.opExtrude","CAP_EDGE",EDGE,{"disambiguationData":[OSD([sQuery(id+"F16.wireOp",EDGE,"E99.left")])],"isStart":false});
            var Q5;
            {var subQ0=sQuery(id+"F16.wireOp",EDGE,"E99.bottom");var subQ1=makeQuery(id+"F16.imprint","INTERSECT",VERTEX,{"derivedFrom":[subQ0,sQuery(id+"F16.wireOp",EDGE,"E100")]});Q5=makeQuery(id+"F17.opExtrude","CAP_EDGE",EDGE,{"disambiguationData":[OSD([subQ0]),TDD([makeQuery(id+"F16.imprint","IMPRINT",EDGE,{"disambiguationData":[TD([[makeQuery(id+"F16.imprint","INTERSECT",VERTEX,{"derivedFrom":[subQ0,sQuery(id+"F16.wireOp",EDGE,"E99.left")]}),-1.0]])],"derivedFrom":subQ0}),makeQuery(id+"F16.imprint","IMPRINT",EDGE,{"disambiguationData":[TD([[subQ1,-1.0]])],"derivedFrom":subQ0})])],"isStart":false});}
            var Q6;
            Q6=makeQuery(id+"F14.opExtrude","SWEPT_EDGE",EDGE,{"disambiguationData":[OSD([sQuery(id+"F13.wireOp",EDGE,"E67.top"),sQuery(id+"F13.wireOp",EDGE,"E67.left")])]});
            var Q7;
            Q7=makeQuery(id+"F14.opExtrude","SWEPT_EDGE",EDGE,{"disambiguationData":[OSD([sQuery(id+"F13.wireOp",EDGE,"E67.bottom"),sQuery(id+"F13.wireOp",EDGE,"E67.left")])]});
            var Q8;
            Q8=makeQuery(id+"F14.opExtrude","SWEPT_EDGE",EDGE,{"disambiguationData":[OSD([sQuery(id+"F13.wireOp",EDGE,"E67.bottom"),sQuery(id+"F13.wireOp",EDGE,"E67.right")])]});
            var Q9;
            Q9=makeQuery(id+"F14.opExtrude","SWEPT_EDGE",EDGE,{"disambiguationData":[OSD([sQuery(id+"F13.wireOp",EDGE,"E67.top"),sQuery(id+"F13.wireOp",EDGE,"E67.right")])]});
            var Q10;
            Q10=makeQuery(id+"F17.opExtrude","SWEPT_EDGE",EDGE,{"disambiguationData":[OSD([sQuery(id+"F16.wireOp",EDGE,"E99.bottom"),sQuery(id+"F16.wireOp",EDGE,"E99.left")])]});
            var Q11;
            Q11=makeQuery(id+"F17.opExtrude","SWEPT_EDGE",EDGE,{"disambiguationData":[OSD([sQuery(id+"F16.wireOp",EDGE,"E99.bottom"),sQuery(id+"F16.wireOp",EDGE,"E99.right")])]});
            var Q12;
            Q12=makeQuery(id+"F17.opExtrude","SWEPT_EDGE",EDGE,{"disambiguationData":[OSD([sQuery(id+"F16.wireOp",EDGE,"E99.top"),sQuery(id+"F16.wireOp",EDGE,"E99.right")])]});
            var Q13;
            Q13=makeQuery(id+"F17.opExtrude","SWEPT_EDGE",EDGE,{"disambiguationData":[OSD([sQuery(id+"F16.wireOp",EDGE,"E99.top"),sQuery(id+"F16.wireOp",EDGE,"E99.left")])]});
            chamfer(context, id + "F18", {"entities" : qUnion([Q0, Q1, Q2, Q3, Q4, Q5, Q6, Q7, Q8, Q9, Q10, Q11, Q12, Q13]), "width" : 1 * mm, "tangentPropagation" : true});
        }
        {
            var Q0;
            Q0=qCreatedBy(makeId("Top.planeOp"),FACE);
            var sketch = newSketch(context, id + "F19", { "sketchPlane" : qUnion([Q0])});
            skLineSegment(sketch, "E135", {"start": v(11.04, 6.04) * mm, "end": v(11.04, 10.04) * mm});
            skLineSegment(sketch, "E136", {"start": v(11.04, 10.04) * mm, "end": v(7.54, 10.04) * mm});
            skLineSegment(sketch, "E137", {"start": v(12.67, -29) * mm, "end": v(26.67, -29) * mm});
            skCircle(sketch, "E138", {"center": v(19.67, -29) * mm, "radius": 7 * mm});
            skSolve(sketch);
        }
        {
            var Q0;
            Q0=sQuery(id+"F19.wireOp",VERTEX,"E138.center");
            var Q1;
            Q1=makeQuery(id+"F11.opExtrude","SWEPT_BODY",BODY,{"disambiguationData":[OSD([sQuery(id+"F10.wireOp",EDGE,"E35.bottom"),sQuery(id+"F10.wireOp",EDGE,"E35.top"),sQuery(id+"F10.wireOp",EDGE,"E35.left"),sQuery(id+"F10.wireOp",EDGE,"E35.right"),sQuery(id+"F10.wireOp",EDGE,"E39.bottom"),sQuery(id+"F10.wireOp",EDGE,"E39.top"),sQuery(id+"F10.wireOp",EDGE,"E39.left"),sQuery(id+"F10.wireOp",EDGE,"E38"),sQuery(id+"F10.wireOp",EDGE,"E41"),sQuery(id+"F10.wireOp",EDGE,"E42"),sQuery(id+"F10.wireOp",EDGE,"E44"),sQuery(id+"F10.wireOp",EDGE,"E45"),sQuery(id+"F10.wireOp",EDGE,"E47"),sQuery(id+"F10.wireOp",EDGE,"E48"),sQuery(id+"F10.wireOp",EDGE,"E50.MirrorCS"),sQuery(id+"F10.wireOp",EDGE,"E51.MirrorCS"),sQuery(id+"F10.wireOp",EDGE,"E52.MirrorCS"),sQuery(id+"F10.wireOp",EDGE,"E53.MirrorCS"),sQuery(id+"F10.wireOp",EDGE,"E54.MirrorCS"),sQuery(id+"F10.wireOp",EDGE,"E59"),sQuery(id+"F10.wireOp",EDGE,"E60")])]});
            hole(context, id + "F20", {"style" : HoleStyle.SIMPLE, "endStyle" : HoleEndStyle.THROUGH, "holeDiameter" : 14 * mm, "majorDiameter" : 5 * mm, "isTappedThrough" : true, "tappedDepth" : 12 * mm, "tapClearance" : 3, "locations" : qUnion([Q0]), "scope" : qUnion([Q1])});
        }
        {
            var Q0;
            {var subQ0=sQuery(id+"F10.wireOp",EDGE,"E36");Q0=makeQuery(id+"F10.imprint","IMPRINT",FACE,{"disambiguationData":[TD([[makeQuery(id+"F10.imprint","IMPRINT",EDGE,{"derivedFrom":subQ0}),-1.0]])]});}
            var Q1;
            {var subQ10=sQuery(id+"F10.wireOp",EDGE,"E36");Q1=makeQuery(id+"F10.imprint","IMPRINT",FACE,{"disambiguationData":[TD([[makeQuery(id+"F10.imprint","IMPRINT",EDGE,{"derivedFrom":subQ10}),1.0]])]});}
            var Q2;
            {var subQ3=sQuery(id+"F10.wireOp",EDGE,"E35.top");Q2=makeQuery(id+"F10.imprint","IMPRINT",FACE,{"disambiguationData":[TD([[makeQuery(id+"F10.imprint","IMPRINT",EDGE,{"derivedFrom":subQ3}),1.0]])]});}
            var Q3;
            {var subQ0=sQuery(id+"F10.wireOp",EDGE,"E50.MirrorCS");Q3=makeQuery(id+"F10.imprint","IMPRINT",FACE,{"disambiguationData":[TD([[makeQuery(id+"F10.imprint","IMPRINT",EDGE,{"derivedFrom":subQ0}),1.0]])]});}
            var Q4;
            {var subQ0=sQuery(id+"F10.wireOp",EDGE,"E42");Q4=makeQuery(id+"F10.imprint","IMPRINT",FACE,{"disambiguationData":[TD([[makeQuery(id+"F10.imprint","IMPRINT",EDGE,{"derivedFrom":subQ0}),-1.0]])]});}
            var Q5;
            {var subQ4=sQuery(id+"F10.wireOp",EDGE,"E53.MirrorCS");Q5=makeQuery(id+"F10.imprint","IMPRINT",FACE,{"disambiguationData":[TD([[makeQuery(id+"F10.imprint","IMPRINT",EDGE,{"derivedFrom":subQ4}),-1.0]])]});}
            var Q6;
            Q6=makeQuery(id+"F10.imprint","IMPRINT",FACE,{"disambiguationData":[TD([[makeQuery(id+"F10.imprint","IMPRINT",EDGE,{"derivedFrom":sQuery(id+"F10.wireOp",EDGE,"E40")}),1.0]])]});
            extrude(context, id + "F21", {"entities" : qUnion([Q0, Q1, Q2, Q3, Q4, Q5, Q6]), "operationType" : NewBodyOperationType.ADD, "oppositeDirection" : true, "depth" : 5 * mm, "offsetDistance" : 25 * mm});
        }
        {
            var Q0;
            Q0=makeQuery(id+"F21.opExtrude","SWEPT_EDGE",EDGE,{"disambiguationData":[OSD([sQuery(id+"F10.wireOp",EDGE,"E35.bottom"),sQuery(id+"F10.wireOp",EDGE,"E35.right")])]});
            var Q1;
            Q1=makeQuery(id+"F21.opExtrude","SWEPT_EDGE",EDGE,{"disambiguationData":[OSD([sQuery(id+"F10.wireOp",EDGE,"E35.top"),sQuery(id+"F10.wireOp",EDGE,"E35.right")])]});
            var Q2;
            Q2=makeQuery(id+"F21.opExtrude","SWEPT_EDGE",EDGE,{"disambiguationData":[OSD([sQuery(id+"F10.wireOp",EDGE,"E35.bottom"),sQuery(id+"F10.wireOp",EDGE,"E35.left")])]});
            var Q3;
            Q3=makeQuery(id+"F21.opExtrude","SWEPT_EDGE",EDGE,{"disambiguationData":[OSD([sQuery(id+"F10.wireOp",EDGE,"E35.top"),sQuery(id+"F10.wireOp",EDGE,"E35.left")])]});
            chamfer(context, id + "F22", {"entities" : qUnion([Q0, Q1, Q2, Q3]), "width" : 1 * mm, "tangentPropagation" : true});
        }
    });
